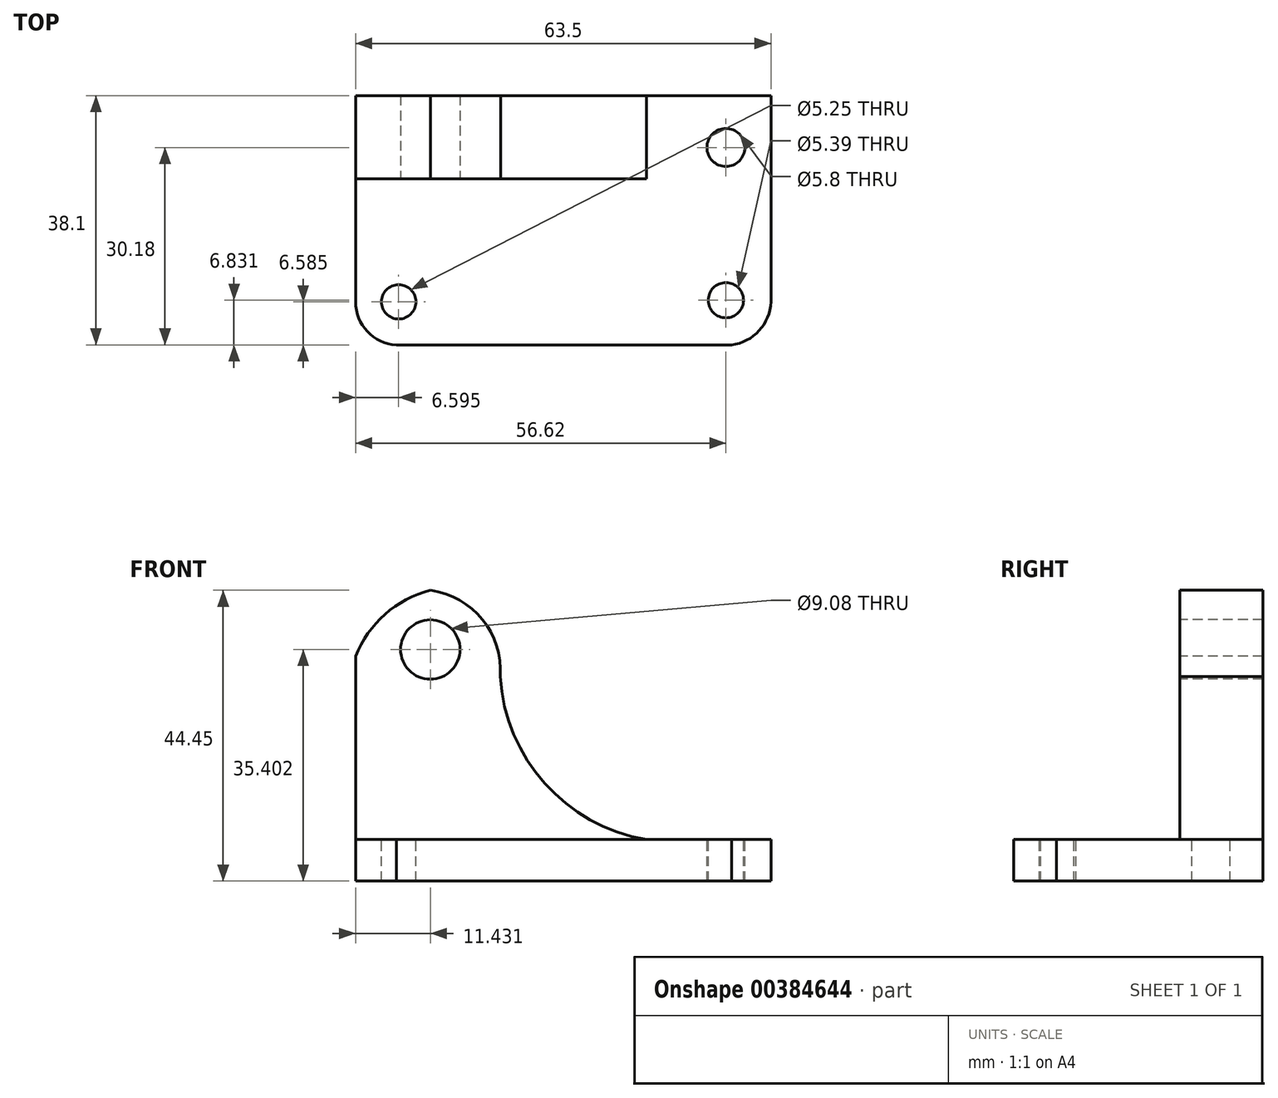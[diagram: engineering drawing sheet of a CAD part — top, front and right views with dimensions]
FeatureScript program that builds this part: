
annotation { "Feature Type Name" : "Feature", "Feature Type Description" : "" }
export const myFeature = defineFeature(function(context is Context, id is Id, definition is map)
    precondition{}
    {
        {
            var Q0;
            Q0=qCreatedBy(makeId("Front.planeOp"),FACE);
            var sketch = newSketch(context, id + "F0", { "sketchPlane" : qUnion([Q0])});
            skLineSegment(sketch, "E0", {"start": v(-28.95, 0) * mm, "end": v(-28.95, 6.35) * mm});
            skLineSegment(sketch, "E1", {"start": v(-28.95, 6.35) * mm, "end": v(34.55, 6.35) * mm});
            skLineSegment(sketch, "E2", {"start": v(34.55, 6.35) * mm, "end": v(34.55, 0) * mm});
            skLineSegment(sketch, "E3", {"start": v(34.55, 0) * mm, "end": v(-28.95, 0) * mm});
            skSolve(sketch);
        }
        {
            var Q0;
            Q0=makeQuery(id+"F0.imprint","IMPRINT",FACE,{"disambiguationData":[TD([[makeQuery(id+"F0.imprint","IMPRINT",EDGE,{"derivedFrom":sQuery(id+"F0.wireOp",EDGE,"E0")}),-1.0]])]});
            extrude(context, id + "F1", {"entities" : qUnion([Q0]), "depth" : 38.1 * mm});
        }
        {
            var Q0;
            Q0=makeQuery(id+"F1.opExtrude","SWEPT_FACE",FACE,{"disambiguationData":[OSD([sQuery(id+"F0.wireOp",EDGE,"E1")])]});
            var sketch = newSketch(context, id + "F2", { "sketchPlane" : qUnion([Q0])});
            skLineSegment(sketch, "E4", {"start": v(-28.95, -12.7) * mm, "end": v(15.5, -12.7) * mm});
            skLineSegment(sketch, "E5", {"start": v(15.5, -12.7) * mm, "end": v(15.5, 0) * mm});
            skLineSegment(sketch, "E6", {"start": v(15.5, 0) * mm, "end": v(-28.95, 0) * mm});
            skLineSegment(sketch, "E7", {"start": v(-28.95, 0) * mm, "end": v(-28.95, -12.7) * mm});
            skSolve(sketch);
        }
        {
            var Q0;
            Q0=makeQuery(id+"F2.imprint","IMPRINT",FACE,{"disambiguationData":[TD([[makeQuery(id+"F2.imprint","IMPRINT",EDGE,{"derivedFrom":sQuery(id+"F2.wireOp",EDGE,"E4")}),1.0]])]});
            extrude(context, id + "F3", {"entities" : qUnion([Q0]), "operationType" : NewBodyOperationType.ADD, "depth" : 38.1 * mm});
        }
        {
            var Q0;
            Q0=makeQuery(id+"F3.opExtrude","SWEPT_FACE",FACE,{"disambiguationData":[OSD([sQuery(id+"F2.wireOp",EDGE,"E4")])]});
            var sketch = newSketch(context, id + "F4", { "sketchPlane" : qUnion([Q0])});
            skArc(sketch, "E8", {"start": v(-17.52, 44.45) * mm, "mid": v(-24.44, 40.78) * mm, "end": v(-28.95, 34.37) * mm});
            skArc(sketch, "E9", {"start": v(-6.82, 31.29) * mm, "mid": v(-9.56, 40) * mm, "end": v(-17.52, 44.45) * mm});
            skArc(sketch, "E10", {"start": v(-6.82, 31.29) * mm, "mid": v(-0.01, 14.92) * mm, "end": v(15.5, 6.35) * mm});
            skCircle(sketch, "E11", {"center": v(-17.52, 35.4) * mm, "radius": 4.54 * mm});
            skSolve(sketch);
        }
        {
            var Q0;
            {var subQ0=sQuery(id+"F4.wireOp",EDGE,"E8");Q0=makeQuery(id+"F4.imprint","IMPRINT",FACE,{"disambiguationData":[TD([[makeQuery(id+"F4.imprint","IMPRINT",EDGE,{"derivedFrom":subQ0}),-1.0]])]});}
            var Q1;
            {var subQ0=sQuery(id+"F4.wireOp",EDGE,"E9");Q1=makeQuery(id+"F4.imprint","IMPRINT",FACE,{"disambiguationData":[TD([[makeQuery(id+"F4.imprint","IMPRINT",EDGE,{"derivedFrom":subQ0}),-1.0]])]});}
            var Q2;
            Q2=makeQuery(id+"F4.imprint","IMPRINT",FACE,{"disambiguationData":[TD([[makeQuery(id+"F4.imprint","IMPRINT",EDGE,{"derivedFrom":sQuery(id+"F4.wireOp",EDGE,"E11")}),1.0]])]});
            extrude(context, id + "F5", {"entities" : qUnion([Q0, Q1, Q2]), "operationType" : NewBodyOperationType.REMOVE, "oppositeDirection" : true, "depth" : 12.7 * mm});
        }
        {
            var Q0;
            Q0=makeQuery(id+"F1.opExtrude","SWEPT_FACE",FACE,{"disambiguationData":[OSD([sQuery(id+"F0.wireOp",EDGE,"E1")])]});
            var sketch = newSketch(context, id + "F6", { "sketchPlane" : qUnion([Q0])});
            skArc(sketch, "E12", {"start": v(-28.95, -31.5) * mm, "mid": v(-27.15, -36.04) * mm, "end": v(-22.72, -38.1) * mm});
            skArc(sketch, "E13", {"start": v(28.52, -38.1) * mm, "mid": v(32.75, -35.92) * mm, "end": v(34.55, -31.52) * mm});
            skCircle(sketch, "E14", {"center": v(-22.36, -31.52) * mm, "radius": 2.63 * mm});
            skCircle(sketch, "E15", {"center": v(27.67, -31.27) * mm, "radius": 2.7 * mm});
            skCircle(sketch, "E16", {"center": v(27.67, -7.92) * mm, "radius": 2.9 * mm});
            skSolve(sketch);
        }
        {
            var Q0;
            Q0=makeQuery(id+"F6.imprint","IMPRINT",FACE,{"disambiguationData":[TD([[makeQuery(id+"F6.imprint","IMPRINT",EDGE,{"derivedFrom":sQuery(id+"F6.wireOp",EDGE,"E14")}),1.0]])]});
            var Q1;
            Q1=makeQuery(id+"F6.imprint","IMPRINT",FACE,{"disambiguationData":[TD([[makeQuery(id+"F6.imprint","IMPRINT",EDGE,{"derivedFrom":sQuery(id+"F6.wireOp",EDGE,"E16")}),1.0]])]});
            var Q2;
            {var subQ0=sQuery(id+"F6.wireOp",EDGE,"E12");var subQ1=sQuery(id+"F0.wireOp",EDGE,"E1");var subQ4=makeQuery(id+"F1.opExtrude","CAP_EDGE",EDGE,{"disambiguationData":[OSD([subQ1])],"isStart":false});var subQ5=makeQuery(id+"F6.imprint","INTERSECT",VERTEX,{"derivedFrom":[subQ4,subQ0]});Q2=makeQuery(id+"F6.imprint","IMPRINT",FACE,{"disambiguationData":[TD([[makeQuery(id+"F6.imprint","IMPRINT",EDGE,{"disambiguationData":[TD([[subQ5,1.0]])],"derivedFrom":subQ0}),-1.0]])]});}
            var Q3;
            {var subQ0=sQuery(id+"F6.wireOp",EDGE,"E13");Q3=makeQuery(id+"F6.imprint","IMPRINT",FACE,{"disambiguationData":[TD([[makeQuery(id+"F6.imprint","IMPRINT",EDGE,{"derivedFrom":subQ0}),-1.0]])]});}
            var Q4;
            Q4=makeQuery(id+"F6.imprint","IMPRINT",FACE,{"disambiguationData":[TD([[makeQuery(id+"F6.imprint","IMPRINT",EDGE,{"derivedFrom":sQuery(id+"F6.wireOp",EDGE,"E15")}),1.0]])]});
            extrude(context, id + "F7", {"entities" : qUnion([Q0, Q1, Q2, Q3, Q4]), "operationType" : NewBodyOperationType.REMOVE, "oppositeDirection" : true, "depth" : 12.7 * mm});
        }
    });
